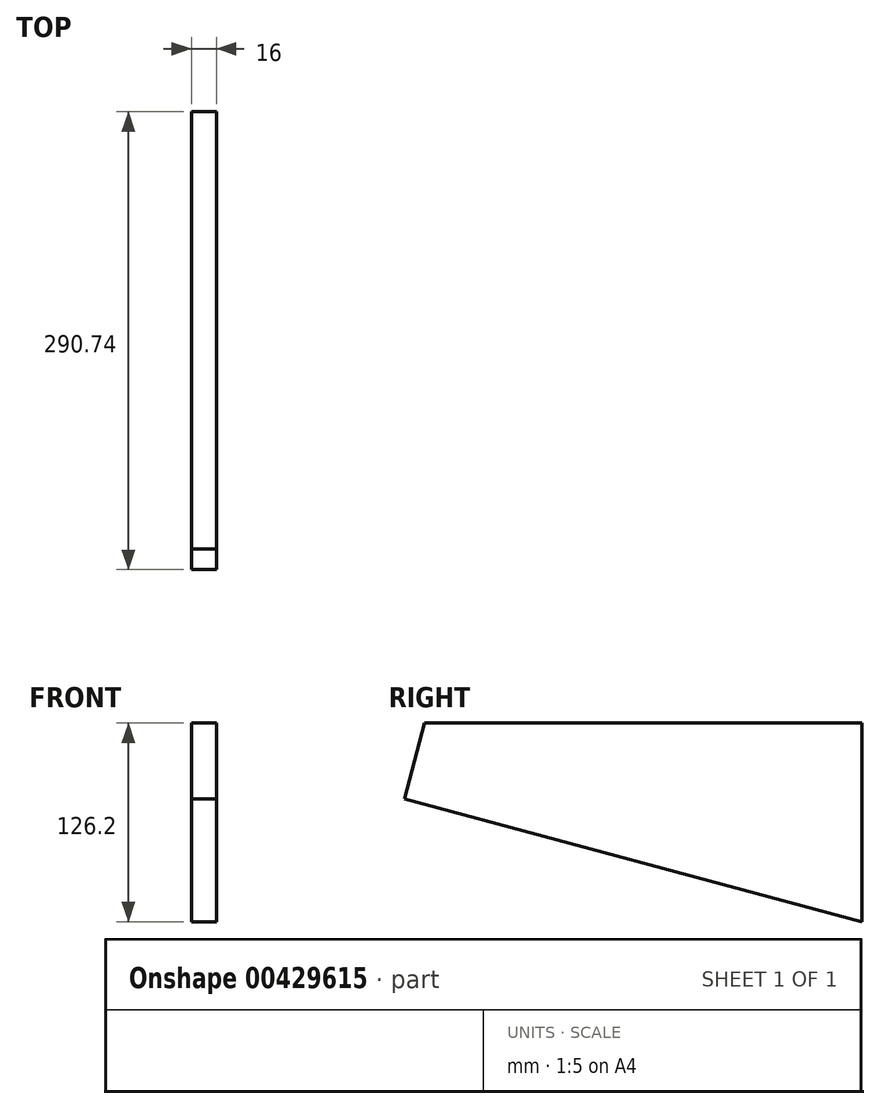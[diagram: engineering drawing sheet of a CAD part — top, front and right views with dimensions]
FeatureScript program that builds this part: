
annotation { "Feature Type Name" : "Feature", "Feature Type Description" : "" }
export const myFeature = defineFeature(function(context is Context, id is Id, definition is map)
    precondition{}
    {
        {
            var Q0;
            Q0=qCreatedBy(makeId("Right.planeOp"),FACE);
            var sketch = newSketch(context, id + "F0", { "sketchPlane" : qUnion([Q0])});
            skLineSegment(sketch, "E0", {"start": v(0, 0) * mm, "end": v(277.8, 0) * mm});
            skLineSegment(sketch, "E1", {"start": v(277.8, 0) * mm, "end": v(277.8, -126.2) * mm});
            skLineSegment(sketch, "E2", {"start": v(277.8, -126.2) * mm, "end": v(-12.94, -48.3) * mm});
            skLineSegment(sketch, "E3", {"start": v(-12.94, -48.3) * mm, "end": v(0, 0) * mm});
            skSolve(sketch);
        }
        {
            var Q0;
            Q0 = qSketchRegion(id + "F0", true);
            extrude(context, id + "F1", {"entities" : qUnion([Q0]), "depth" : 16 * mm});
        }
    });
